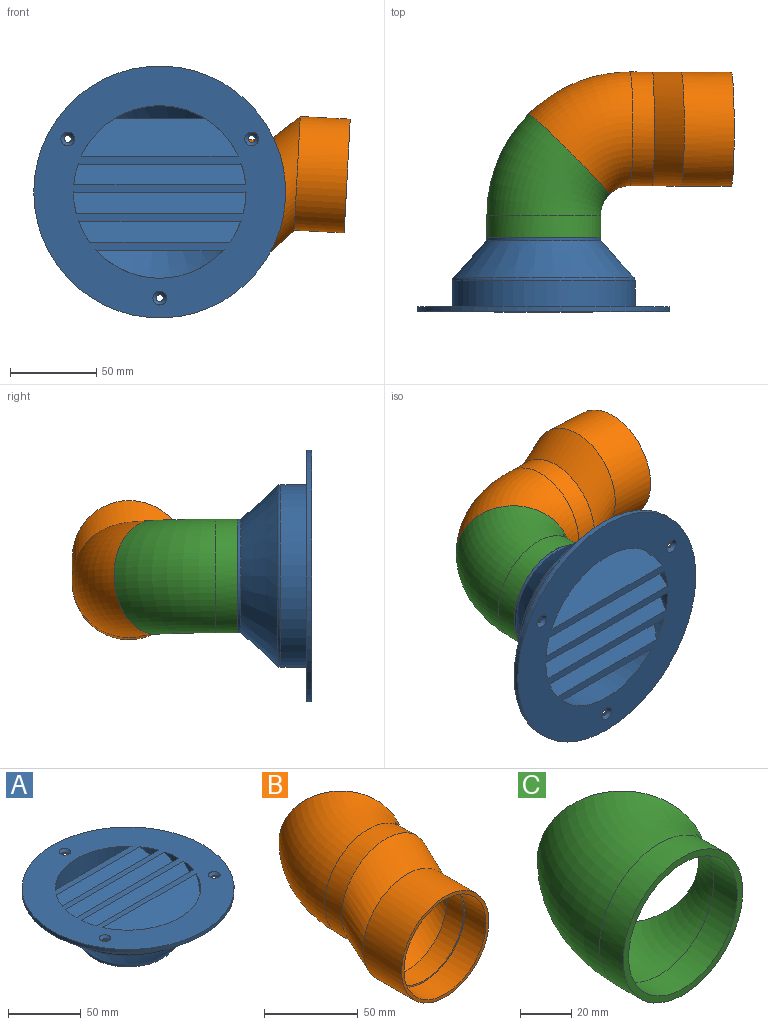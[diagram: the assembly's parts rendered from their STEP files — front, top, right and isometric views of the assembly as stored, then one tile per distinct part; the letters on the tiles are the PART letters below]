
ASSEMBLY  parts=3 mates=3
PART A: 36 faces, bbox 146x146x43 mm
  f0: cylinder r=50mm len=33.48mm, axis (0,0,-1), area 226.7mm2, adj f8,f18,f32,f33
  f1: cylinder r=50mm len=33.48mm, axis (0,0,-1), area 219.7mm2, adj f8,f18,f29,f30
  f2: cylinder r=50mm len=33.48mm, axis (0,0,-1), area 243.7mm2, adj f8,f18,f25,f27
  f3: cylinder r=50mm len=90.88mm, axis (0,0,-1), area 1576.4mm2, adj f8,f18,f26
  f4: cylinder r=50mm len=96.85mm, axis (0,0,-1), area 1950.1mm2, adj f8,f18,f35
  f5: cylinder r=50mm len=33.48mm, axis (0,0,-1), area 226.7mm2, adj f8,f18,f32,f33
  f6: cylinder r=50mm len=33.48mm, axis (0,0,-1), area 219.7mm2, adj f8,f18,f29,f30
  f7: cylinder r=50mm len=33.48mm, axis (0,0,-1), area 243.7mm2, adj f8,f18,f25,f27
  f8: plane 146x146mm, normal (0,0,1), area 10443.2mm2, adj f0,f1,f2,f3,f4,f5,f6,f7
  f9: cone r=2mm half-angle=45deg, axis (0,0,1), area 53.3mm2, adj f8,f13
  f10: cylinder r=73mm len=146mm, axis (0,0,-1), area 1376mm2, adj f8,f14
  f11: cone r=2mm half-angle=45deg, axis (0,0,1), area 53.3mm2, adj f8,f15
  f12: cone r=2mm half-angle=45deg, axis (0,0,1), area 53.3mm2, adj f8,f16
  f13: cylinder r=2mm len=4mm, axis (0,0,1), area 12.6mm2, adj f9,f14
  f14: plane 146x146mm, normal (0,0,-1), area 7879.1mm2, adj f10,f13,f15,f16,f17
  f15: cylinder r=2mm len=4mm, axis (0,0,1), area 12.6mm2, adj f11,f14
  f16: cylinder r=2mm len=4mm, axis (0,0,1), area 12.6mm2, adj f12,f14
  f17: cylinder r=53mm len=106mm, axis (0,0,1), area 4995.1mm2, adj f14,f19
  f18: cone r=30mm half-angle=42.3deg, axis (0,0,1), area 7472.5mm2, adj f0,f1,f2,f3,f4,f5,f6,f7
  f19: torus R=50mm, axis (0,0,1), area 733.4mm2, adj f17,f21
  f20: cylinder r=30mm len=60mm, axis (0,0,1), area 565.5mm2, adj f18,f22
  f21: cone r=32.22mm half-angle=42.3deg, axis (0,0,1), area 7649.6mm2, adj f19,f23
  f22: plane 66x66mm, normal (0,0,-1), area 593.8mm2, adj f20,f23
  f23: cylinder r=33mm len=66mm, axis (0,0,1), area 381.6mm2, adj f21,f22
  f24: plane 65.82x4.67mm, normal (0,0,-1), area 279.5mm2, adj f18,f25,f26
  f25: plane 94.61x21.45mm, normal (0,0.64,-0.77), area 2322.8mm2, adj f2,f7,f8,f24
  f26: plane 90.88x21.45mm, normal (0,-0.64,0.77), area 2122.1mm2, adj f3,f8,f24
  f27: plane 99.65x21.45mm, normal (0,-0.64,0.77), area 2648.4mm2, adj f2,f7,f8,f28
  f28: plane 90.8x4.67mm, normal (0,0,-1), area 412.8mm2, adj f18,f27,f29
  f29: plane 100x21.45mm, normal (0,0.64,-0.77), area 2718.1mm2, adj f1,f6,f8,f28
  f30: plane 100x21.45mm, normal (0,-0.64,0.77), area 2776.8mm2, adj f1,f6,f8,f31
  f31: plane 99.64x4.67mm, normal (0,0,-1), area 462.5mm2, adj f18,f30,f32
  f32: plane 100x21.45mm, normal (0,0.64,-0.77), area 2754.5mm2, adj f0,f5,f8,f31
  f33: plane 98.78x21.45mm, normal (0,-0.64,0.77), area 2574mm2, adj f0,f5,f8,f34
  f34: plane 98.78x4.67mm, normal (0,0,-1), area 456.9mm2, adj f18,f33,f35
  f35: plane 96.85x21.45mm, normal (0,0.64,-0.77), area 2449.6mm2, adj f4,f8,f34
PART B: 12 faces, bbox 88.5x127.5x101.5 mm
  f0: torus R=50mm, axis (0,0,-1), area 7402.2mm2, adj f1,f2
  f1: cylinder r=30mm len=60mm, axis (0,1,0), area 2450.4mm2, adj f0,f4
  f2: plane 66x46.67mm, normal (0.71,0.71,0), area 593.8mm2, adj f0,f3
  f3: torus R=50mm, axis (0,0,-1), area 8142.4mm2, adj f2,f5
  f4: bspline ~95.45x74.71mm, area 3597mm2, adj f1,f6
  f5: cylinder r=33mm len=66mm, axis (0,1,0), area 2695.5mm2, adj f3,f8
  f6: cylinder r=30mm len=60mm, axis (0,1,0), area 2450.4mm2, adj f4,f7
  f7: plane 62x62mm, normal (0,-1,0), area 191.6mm2, adj f6,f9
  f8: offset ~83.78x66.17mm, area 4010.5mm2, adj f5,f10
  f9: cylinder r=31mm len=62mm, axis (0,-1,0), area 3116.5mm2, adj f7,f11
  f10: cylinder r=33mm len=66mm, axis (0,1,0), area 6013mm2, adj f8,f11
  f11: plane 66x66mm, normal (0,-1,0), area 402.1mm2, adj f9,f10
PART C: 6 faces, bbox 77.8x76.5x66 mm
  f0: cylinder r=30mm len=60mm, axis (0,1,0), area 2450.4mm2, adj f1,f4
  f1: torus R=50mm, axis (0,0,-1), area 7402.2mm2, adj f0,f2
  f2: plane 66x46.67mm, normal (0.71,0.71,0), area 593.8mm2, adj f1,f3
  f3: torus R=50mm, axis (0,0,-1), area 8142.4mm2, adj f2,f5
  f4: plane 66x66mm, normal (0,-1,0), area 593.8mm2, adj f0,f5
  f5: cylinder r=33mm len=66mm, axis (0,1,0), area 2695.5mm2, adj f3,f4
PLACE A rot(axis=(0,-0.71,0.71),180deg) t=(27.55,16.75,-54.69)mm fixed
PLACE B rot(axis=(0.71,-0.71,-0.02),177.8deg) t=(87.47,79.75,-57.87)mm
PLACE C rot(axis=(0,1,0),3deg) t=(27.55,16.75,-54.69)mm
MATE fastened C.f2 <-> B.f2  axis (0.71,0.71,-0.04) through (42.17,65.11,-55.46)mm
MATE revolute C.f0 <-> C.f1  axis (0,-1,0) through (27.55,16.75,-54.69)mm
MATE revolute A.f20 <-> C.f0  axis (0,1,0) through (27.55,16.75,-54.69)mm
